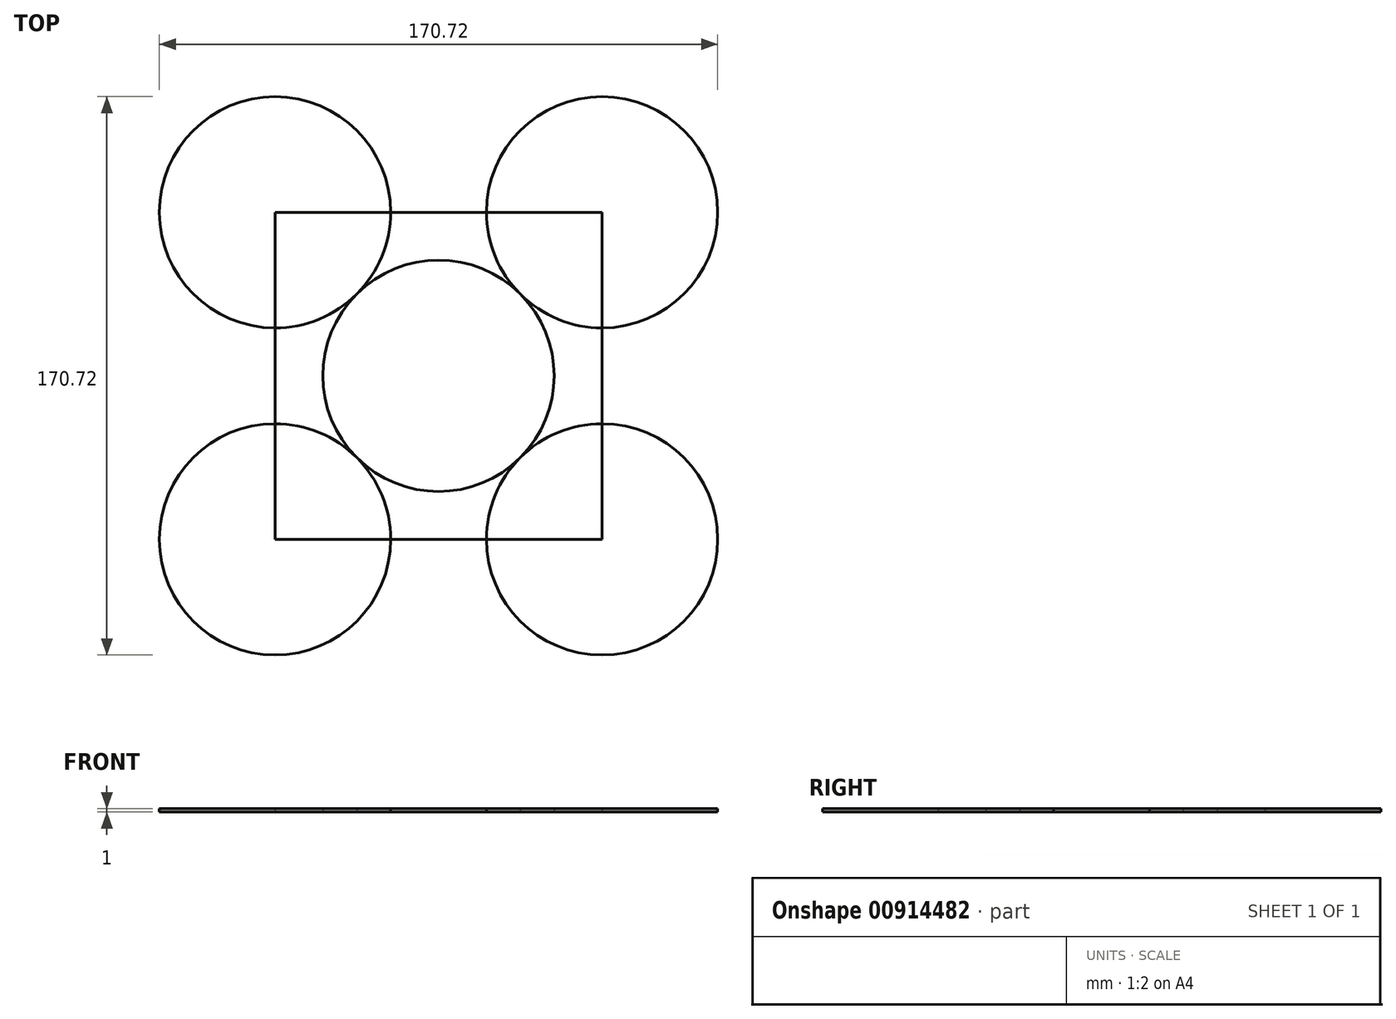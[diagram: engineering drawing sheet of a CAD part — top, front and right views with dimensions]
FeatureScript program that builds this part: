
annotation { "Feature Type Name" : "Feature", "Feature Type Description" : "" }
export const myFeature = defineFeature(function(context is Context, id is Id, definition is map)
    precondition{}
    {
        {
            var Q0;
            Q0=qCreatedBy(makeId("Top.planeOp"),FACE);
            var sketch = newSketch(context, id + "F0", { "sketchPlane" : qUnion([Q0])});
            skLineSegment(sketch, "E0.bottom", {"start": v(50, 50) * mm, "end": v(-50, 50) * mm});
            skLineSegment(sketch, "E0.top", {"start": v(50, -50) * mm, "end": v(-50, -50) * mm});
            skLineSegment(sketch, "E0.left", {"start": v(50, 50) * mm, "end": v(50, -50) * mm});
            skLineSegment(sketch, "E0.right", {"start": v(-50, 50) * mm, "end": v(-50, -50) * mm});
            skPoint(sketch, "E0.middle", {"position": v(0, 0) * mm});
            skCircle(sketch, "E1", {"center": v(50, 50) * mm, "radius": 35.36 * mm});
            skCircle(sketch, "E2", {"center": v(-50, 50) * mm, "radius": 35.36 * mm});
            skCircle(sketch, "E3", {"center": v(-50, -50) * mm, "radius": 35.36 * mm});
            skCircle(sketch, "E4", {"center": v(50, -50) * mm, "radius": 35.36 * mm});
            skCircle(sketch, "E5", {"center": v(0, 0) * mm, "radius": 35.36 * mm});
            skSolve(sketch);
        }
        {
            var Q0;
            {var subQ0=sQuery(id+"F0.wireOp",EDGE,"E0.right");var subQ1=sQuery(id+"F0.wireOp",EDGE,"E0.bottom");var subQ2=makeQuery(id+"F0.imprint","INTERSECT",VERTEX,{"derivedFrom":[subQ1,subQ0]});Q0=makeQuery(id+"F0.imprint","IMPRINT",FACE,{"disambiguationData":[TD([[makeQuery(id+"F0.imprint","IMPRINT",EDGE,{"disambiguationData":[TD([[subQ2,1.0]])],"derivedFrom":subQ1}),-1.0]])]});}
            var Q1;
            {var subQ0=sQuery(id+"F0.wireOp",EDGE,"E0.left");var subQ1=sQuery(id+"F0.wireOp",EDGE,"E0.bottom");var subQ2=makeQuery(id+"F0.imprint","INTERSECT",VERTEX,{"derivedFrom":[subQ1,subQ0]});Q1=makeQuery(id+"F0.imprint","IMPRINT",FACE,{"disambiguationData":[TD([[makeQuery(id+"F0.imprint","IMPRINT",EDGE,{"disambiguationData":[TD([[subQ2,-1.0]])],"derivedFrom":subQ1}),-1.0]])]});}
            var Q2;
            {var subQ0=sQuery(id+"F0.wireOp",EDGE,"E1");var subQ1=sQuery(id+"F0.wireOp",EDGE,"E0.bottom");var subQ2=makeQuery(id+"F0.imprint","INTERSECT",VERTEX,{"derivedFrom":[subQ1,subQ0]});Q2=makeQuery(id+"F0.imprint","IMPRINT",FACE,{"disambiguationData":[TD([[makeQuery(id+"F0.imprint","IMPRINT",EDGE,{"disambiguationData":[TD([[subQ2,-1.0]])],"derivedFrom":subQ1}),1.0]])]});}
            var Q3;
            {var subQ0=sQuery(id+"F0.wireOp",EDGE,"E1");var subQ1=sQuery(id+"F0.wireOp",EDGE,"E0.left");var subQ2=makeQuery(id+"F0.imprint","INTERSECT",VERTEX,{"derivedFrom":[subQ1,subQ0]});Q3=makeQuery(id+"F0.imprint","IMPRINT",FACE,{"disambiguationData":[TD([[makeQuery(id+"F0.imprint","IMPRINT",EDGE,{"disambiguationData":[TD([[subQ2,-1.0]])],"derivedFrom":subQ1}),-1.0]])]});}
            var Q4;
            {var subQ0=sQuery(id+"F0.wireOp",EDGE,"E2");var subQ1=sQuery(id+"F0.wireOp",EDGE,"E0.right");var subQ2=makeQuery(id+"F0.imprint","INTERSECT",VERTEX,{"derivedFrom":[subQ1,subQ0]});Q4=makeQuery(id+"F0.imprint","IMPRINT",FACE,{"disambiguationData":[TD([[makeQuery(id+"F0.imprint","IMPRINT",EDGE,{"disambiguationData":[TD([[subQ2,-1.0]])],"derivedFrom":subQ1}),1.0]])]});}
            var Q5;
            {var subQ0=sQuery(id+"F0.wireOp",EDGE,"E4");var subQ1=sQuery(id+"F0.wireOp",EDGE,"E0.top");var subQ2=makeQuery(id+"F0.imprint","INTERSECT",VERTEX,{"derivedFrom":[subQ1,subQ0]});Q5=makeQuery(id+"F0.imprint","IMPRINT",FACE,{"disambiguationData":[TD([[makeQuery(id+"F0.imprint","IMPRINT",EDGE,{"disambiguationData":[TD([[subQ2,-1.0]])],"derivedFrom":subQ1}),-1.0]])]});}
            var Q6;
            {var subQ0=sQuery(id+"F0.wireOp",EDGE,"E0.right");var subQ1=sQuery(id+"F0.wireOp",EDGE,"E0.top");var subQ2=makeQuery(id+"F0.imprint","INTERSECT",VERTEX,{"derivedFrom":[subQ1,subQ0]});Q6=makeQuery(id+"F0.imprint","IMPRINT",FACE,{"disambiguationData":[TD([[makeQuery(id+"F0.imprint","IMPRINT",EDGE,{"disambiguationData":[TD([[subQ2,1.0]])],"derivedFrom":subQ1}),1.0]])]});}
            var Q7;
            {var subQ0=sQuery(id+"F0.wireOp",EDGE,"E0.left");var subQ1=sQuery(id+"F0.wireOp",EDGE,"E0.top");var subQ2=makeQuery(id+"F0.imprint","INTERSECT",VERTEX,{"derivedFrom":[subQ1,subQ0]});Q7=makeQuery(id+"F0.imprint","IMPRINT",FACE,{"disambiguationData":[TD([[makeQuery(id+"F0.imprint","IMPRINT",EDGE,{"disambiguationData":[TD([[subQ2,-1.0]])],"derivedFrom":subQ1}),1.0]])]});}
            extrude(context, id + "F1", {"entities" : qUnion([Q0, Q1, Q2, Q3, Q4, Q5, Q6, Q7]), "depth" : 1 * mm, "offsetDistance" : 25 * mm});
        }
    });
